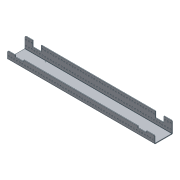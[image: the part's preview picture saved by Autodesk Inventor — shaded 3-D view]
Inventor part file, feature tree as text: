
AUTODESK INVENTOR PART (.ipt)
format: ipt  version: 2016 (Build 200138000, 138)  size: 380,416 bytes
history: native  units: in
note: dims shown in document units (in); Inventor stores cm internally (conversion verified against a paired STEP export)
features: extrude x1, sketch x1, other x1
ambient origin geometry x8: Origin, YZ Plane, XZ Plane, XY Plane, X Axis, Y Axis, Z Axis, Center Point
bodies: Solid1 (feature_tree)
feature tree (3):
  extrude  "Extrusion2"  Depth=0.3in
  sketch  "Sketch2"  dims[d7=0.2in d8=0.2in d9=0.2in d10=0.2in d11=0.3in d12=0.3in d13=5.0in d14=0.0in]
  other  "_AM14U3 End Sheet Rev1_-_LPattern4_"
